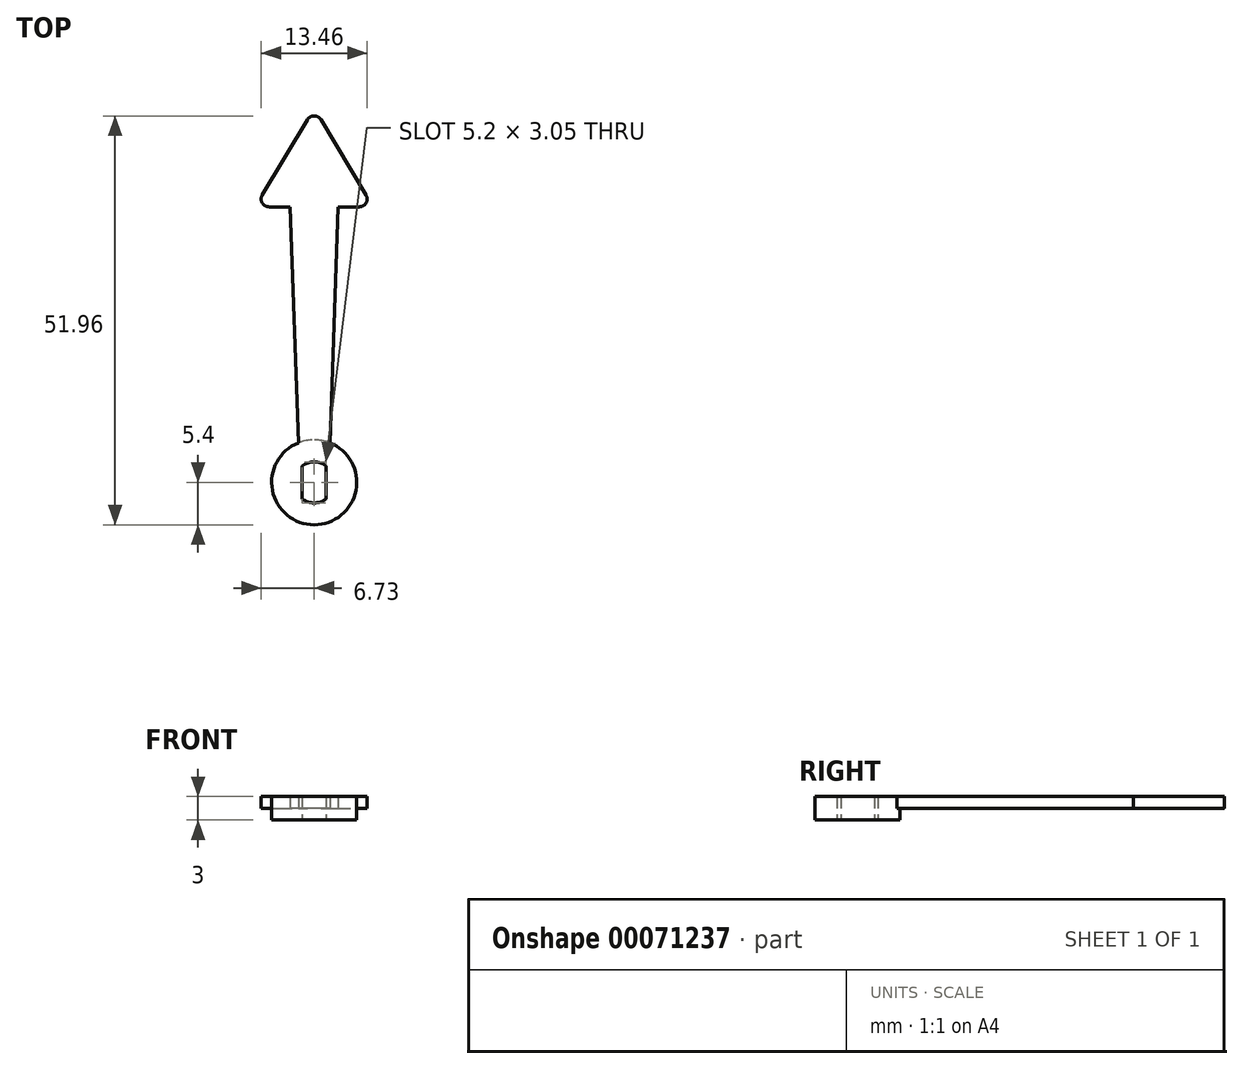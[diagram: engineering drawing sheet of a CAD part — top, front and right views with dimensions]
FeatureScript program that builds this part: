
annotation { "Feature Type Name" : "Feature", "Feature Type Description" : "" }
export const myFeature = defineFeature(function(context is Context, id is Id, definition is map)
    precondition{}
    {
        {
            var Q0;
            Q0=qCreatedBy(makeId("Top.planeOp"),FACE);
            var sketch = newSketch(context, id + "F0", { "sketchPlane" : qUnion([Q0])});
            skCircle(sketch, "E0", {"center": v(0, 0) * mm, "radius": 2.6 * mm});
            skCircle(sketch, "E1", {"center": v(0, 0) * mm, "radius": 5.4 * mm});
            skLineSegment(sketch, "E2", {"start": v(-1.52, 2.1) * mm, "end": v(-1.53, -2.1) * mm});
            skLineSegment(sketch, "E3", {"start": v(1.52, 2.1) * mm, "end": v(1.52, -2.1) * mm});
            skSolve(sketch);
        }
        {
            var Q0;
            Q0=makeQuery(id+"F0.imprint","IMPRINT",FACE,{"disambiguationData":[TD([[makeQuery(id+"F0.imprint","IMPRINT",EDGE,{"derivedFrom":sQuery(id+"F0.wireOp",EDGE,"E1")}),1.0]])]});
            var Q1;
            {var subQ0=sQuery(id+"F0.wireOp",EDGE,"E2");Q1=makeQuery(id+"F0.imprint","IMPRINT",FACE,{"disambiguationData":[TD([[makeQuery(id+"F0.imprint","IMPRINT",EDGE,{"derivedFrom":subQ0}),-1.0]])]});}
            var Q2;
            {var subQ0=sQuery(id+"F0.wireOp",EDGE,"E3");Q2=makeQuery(id+"F0.imprint","IMPRINT",FACE,{"disambiguationData":[TD([[makeQuery(id+"F0.imprint","IMPRINT",EDGE,{"derivedFrom":subQ0}),1.0]])]});}
            extrude(context, id + "F1", {"entities" : qUnion([Q0, Q1, Q2]), "endBound" : BoundingType.SYMMETRIC, "depth" : 3 * mm});
        }
        {
            var Q0;
            Q0=qCreatedBy(makeId("Top.planeOp"),FACE);
            var sketch = newSketch(context, id + "F2", { "sketchPlane" : qUnion([Q0])});
            skLineSegment(sketch, "E4", {"start": v(0, 0) * mm, "end": v(0, 35) * mm, "construction": true});
            skLineSegment(sketch, "E5", {"start": v(0, 5.02) * mm, "end": v(2, 5.02) * mm});
            skLineSegment(sketch, "E6", {"start": v(0, 35) * mm, "end": v(3.05, 35) * mm});
            skLineSegment(sketch, "E7", {"start": v(2, 5.02) * mm, "end": v(3.05, 35) * mm});
            skLineSegment(sketch, "E8.MirrorCS", {"start": v(0, 35) * mm, "end": v(-3.05, 35) * mm});
            skLineSegment(sketch, "E9.MirrorCS", {"start": v(-2, 5.02) * mm, "end": v(-3.05, 35) * mm});
            skLineSegment(sketch, "E10.MirrorCS", {"start": v(0, 5.02) * mm, "end": v(-2, 5.02) * mm});
            skSolve(sketch);
        }
        {
            var Q0;
            Q0=makeQuery(id+"F2.imprint","IMPRINT",FACE,{"disambiguationData":[TD([[makeQuery(id+"F2.imprint","IMPRINT",EDGE,{"derivedFrom":sQuery(id+"F2.wireOp",EDGE,"E5")}),1.0]])]});
            var Q1;
            Q1=makeQuery(id+"F1.opExtrude","CAP_FACE",FACE,{"disambiguationData":[OSD([sQuery(id+"F0.wireOp",EDGE,"E0"),sQuery(id+"F0.wireOp",EDGE,"E1"),sQuery(id+"F0.wireOp",EDGE,"E2"),sQuery(id+"F0.wireOp",EDGE,"E3")])],"isStart":false});
            extrude(context, id + "F3", {"entities" : qUnion([Q0]), "operationType" : NewBodyOperationType.ADD, "endBound" : BoundingType.UP_TO_SURFACE, "endBoundEntityFace" : qUnion([Q1]), "depth" : 25.4 * mm});
        }
        {
            var Q0;
            Q0=qCreatedBy(makeId("Top.planeOp"),FACE);
            var sketch = newSketch(context, id + "F4", { "sketchPlane" : qUnion([Q0])});
            skLineSegment(sketch, "E11", {"start": v(0, 35) * mm, "end": v(0, 47.5) * mm, "construction": true});
            skSolve(sketch);
        }
        {
            var Q0;
            Q0=qCreatedBy(makeId("Top.planeOp"),FACE);
            var sketch = newSketch(context, id + "F5", { "sketchPlane" : qUnion([Q0])});
            skLineSegment(sketch, "E12", {"start": v(-7.5, 35) * mm, "end": v(7.5, 35) * mm});
            skLineSegment(sketch, "E13", {"start": v(-7.5, 35) * mm, "end": v(0, 47.5) * mm});
            skLineSegment(sketch, "E14", {"start": v(0, 47.5) * mm, "end": v(7.5, 35) * mm});
            skSolve(sketch);
        }
        {
            var Q0;
            Q0=makeQuery(id+"F5.imprint","IMPRINT",FACE,{"disambiguationData":[TD([[makeQuery(id+"F5.imprint","IMPRINT",EDGE,{"derivedFrom":sQuery(id+"F5.wireOp",EDGE,"E12")}),1.0]])]});
            var Q1;
            Q1=makeQuery(id+"F3.boolean.opBoolean","MERGE",FACE,{"derivedFrom":[makeQuery(id+"F1.opExtrude","CAP_FACE",FACE,{"disambiguationData":[OSD([sQuery(id+"F0.wireOp",EDGE,"E0"),sQuery(id+"F0.wireOp",EDGE,"E1"),sQuery(id+"F0.wireOp",EDGE,"E2"),sQuery(id+"F0.wireOp",EDGE,"E3")])],"isStart":false}),makeQuery(id+"F3.opExtrude","CAP_FACE",FACE,{"disambiguationData":[OSD([sQuery(id+"F2.wireOp",EDGE,"E5"),sQuery(id+"F2.wireOp",EDGE,"E6"),sQuery(id+"F2.wireOp",EDGE,"E7"),sQuery(id+"F2.wireOp",EDGE,"E8.MirrorCS"),sQuery(id+"F2.wireOp",EDGE,"E9.MirrorCS"),sQuery(id+"F2.wireOp",EDGE,"E10.MirrorCS")])],"isStart":false})]});
            extrude(context, id + "F6", {"entities" : qUnion([Q0]), "operationType" : NewBodyOperationType.ADD, "endBound" : BoundingType.UP_TO_SURFACE, "endBoundEntityFace" : qUnion([Q1]), "depth" : 25.4 * mm});
        }
        {
            var Q0;
            Q0=makeQuery(id+"F6.opExtrude","SWEPT_EDGE",EDGE,{"disambiguationData":[OSD([sQuery(id+"F5.wireOp",EDGE,"E13"),sQuery(id+"F5.wireOp",EDGE,"E14")])]});
            var Q1;
            Q1=makeQuery(id+"F6.opExtrude","SWEPT_EDGE",EDGE,{"disambiguationData":[OSD([sQuery(id+"F5.wireOp",EDGE,"E12"),sQuery(id+"F5.wireOp",EDGE,"E13")])]});
            var Q2;
            Q2=makeQuery(id+"F6.opExtrude","SWEPT_EDGE",EDGE,{"disambiguationData":[OSD([sQuery(id+"F5.wireOp",EDGE,"E12"),sQuery(id+"F5.wireOp",EDGE,"E14")])]});
            fillet(context, id + "F7", {"entities" : qUnion([Q0, Q1, Q2]), "radius" : 1 * mm, "tangentPropagation" : true, "allowEdgeOverflow" : false});
        }
    });
